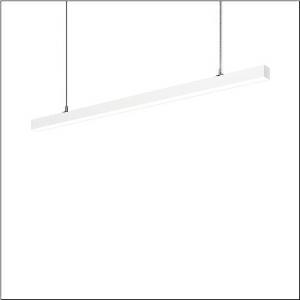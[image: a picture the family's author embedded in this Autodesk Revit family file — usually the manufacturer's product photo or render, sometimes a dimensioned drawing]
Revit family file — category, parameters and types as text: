
# Revit family: silica_21_51mx30db45wb
name_source: partatom
category: Lighting Fixtures
units: mm (PartAtom-declared; Revit-internal decimal feet)

## family parameters
Cut with Voids When Loaded = No
Host = Face
Light Source = No
Part Type = Normal
Room Calculation Point = No
Round Connector Dimension = Use Diameter
Shared = No

## types (1)
- --- (1 x LED, 5260 lm, 32 W, 4000K)
    Apparent Load = 32 VA
    CIE Flux Codes = 47 79 96 57 100
    Color Rendering = 80
    Color Temperature = 4000K
    Default Elevation = 1800 mm
    Description = Silica 21, office luminaire, primary optical cover: cover, of PMMA, opal, light emission: direct/indirect distribution, primary light characteristic: symmetric, installation type: suspended mounting, LED, rated luminous flux: 5.260lm, luminous efficacy: 164lm/W, light colour: 840, colour temperature: 4000K, control gear: DALI 2, with terminal, 3+2-pole, max. 2.5mm², mains connection: 220..240V, AC, 50/60Hz, rated input power: 32W, luminaire housing, of aluminium, traffic white (RAL 9016), length: 1.504mm, width: 53mm, height: 53mm, protection rating (complete): IP20, insulation class (complete): insulation class I (protective earthing), certification: CE, permissible operating ambient temperature: 0..+35°C, standard: EN 50419, packaging unit: 1 piece
    Height = 53 mm
    Lamp = 1 x LED
    Lamp Light Flux = 5260 lm
    Lamp Power = 32 W
    Lamp count = 1
    Length = 1504 mm
    Luminous efficacy = 164 lm/W
    Manufacturer = Siteco
    ModVariant = No
    Model = 51MX30DB45WB
    Mounting Place = Ceiling
    Mounting Type = Pendant
    Number of Poles = 1
    OnlyDefault = Yes
    Power Factor = 1
    Product Name = Silica 21
    Product group = office luminaire | ceiling pendant
    ProductGroupID = 903
    Protection Class = Protection class I
    Protection Degree = IP 20
    RLX_Detail_Level = 1
    RLX_Emergency_Light_Flux = 0 lm
    RLX_Emergency_Type = 0
    RLX_Emergency_Type_DB = No
    RlxData = <blob elided: 18377 chars, md5=549573d1>
    Socket = socket
    Standby Power = 0 W
    System Light Flux = 5260 lm
    System Power = 32 W
    Type Comments = factory setting: luminous flux: 100 % | dim-lin: 254 | 218 mA
    Type Image = l_1349027.jpg
    URL = http://relux.com
    VarID = @adj_116977
    Voltage = 0 V
    Weight = 0.00 kg
    Width = 53 mm

## geometry (parser evidence)
native form markers: Blend x4, Sweep x12
no freeform markers — native parametric forms only
